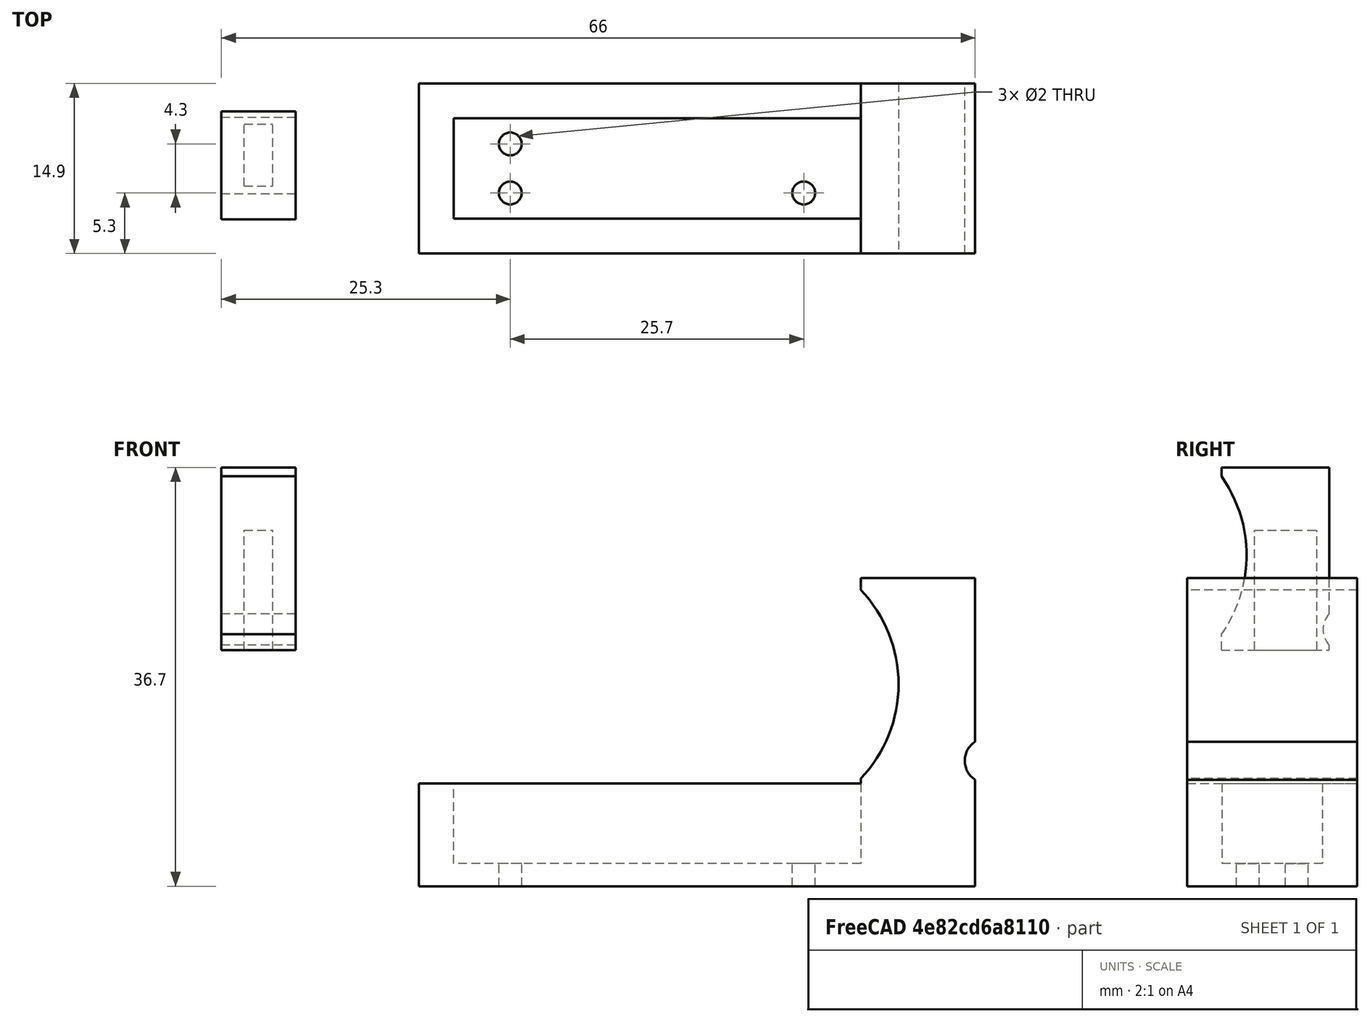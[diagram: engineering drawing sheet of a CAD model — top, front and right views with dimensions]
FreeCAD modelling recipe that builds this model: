
FCSTD DOCUMENT  (FreeCAD 0.18.4R)
Label: LDS_bracket_v1
License: All rights reserved
LicenseURL: http://en.wikipedia.org/wiki/All_rights_reserved
objects: Part::Cut×7, Part::Cylinder×7, Part::Box×6, Part::MultiFuse×2
note: 22 computed .brp shape members not serialized (recipe doc carries the construction recipe); baked Part::Feature solids carry a one-line shape summary decoded from their .brp

FEATURE [Part::Box] Box  label="Cube"
  AttacherType = Attacher::AttachEngine3D
  Height = 10
  Length = 36.6
  Placement = pos=(0.05,0.05,-2) rot=(0,0,1;0rad)
  Width = 8.8
FEATURE [Part::Box] Box001  label="Cube001"
  AttacherType = Attacher::AttachEngine3D
  Height = 7
  Length = 45.7
  Placement = pos=(-3,-3,0) rot=(0,0,1;0rad)
  Width = 14.9
FEATURE [Part::Cut] Cut
  Base = -> Box001
  Tool = -> Box
FEATURE [Part::Box] Box004  label="Cube004"
  AttacherType = Attacher::AttachEngine3D
  Height = 2
  Length = 45.7
  Placement = pos=(-3,-3,-2) rot=(0,0,1;0rad)
  Width = 14.9
FEATURE [Part::Cylinder] Cylinder
  Angle = 360
  AttacherType = Attacher::AttachEngine3D
  Height = 10
  Placement = pos=(5,2.3,-4) rot=(0,0,1;0rad)
  Radius = 1
FEATURE [Part::Cylinder] Cylinder002
  Angle = 360
  AttacherType = Attacher::AttachEngine3D
  Height = 10
  Placement = pos=(5,6.6,-4) rot=(0,0,1;0rad)
  Radius = 1
FEATURE [Part::Cylinder] Cylinder003
  Angle = 360
  AttacherType = Attacher::AttachEngine3D
  Height = 10
  Placement = pos=(30.7,2.3,-4) rot=(0,0,1;0rad)
  Radius = 1
FEATURE [Part::Box] Box005  label="Cube005"
  AttacherType = Attacher::AttachEngine3D
  Height = 27
  Length = 10
  Placement = pos=(35.7,-3,-2) rot=(0,0,1;0rad)
  Width = 14.9
FEATURE [Part::Cylinder] Cylinder004
  Angle = 360
  AttacherType = Attacher::AttachEngine3D
  Height = 20
  Placement = pos=(27,14,15.7) rot=(1,0,0;1.5708rad)
  Radius = 12
FEATURE [Part::Cut] Cut001
  Base = -> Box005
  Tool = -> Cylinder004
FEATURE [Part::Cylinder] Cylinder005
  Angle = 360
  AttacherType = Attacher::AttachEngine3D
  Height = 16
  Placement = pos=(46.8,-3.5,9) rot=(-1,0,0;1.5708rad)
  Radius = 2
FEATURE [Part::Cut] Cut002
  Base = -> Cut001
  Tool = -> Cylinder005
FEATURE [Part::MultiFuse] Fusion
  Shapes = -> [Cylinder,Cylinder002,Cylinder003]
FEATURE [Part::MultiFuse] Fusion001
  Shapes = -> [Cut,Cut002,Box004]
FEATURE [Part::Cut] Cut003
  Base = -> Fusion001
  Tool = -> Fusion
FEATURE [Part::Box] Box007  label="Cube007"
  AttacherType = Attacher::AttachEngine3D
  Height = 10.5
  Length = 2.5
  Placement = pos=(-18.3,2.9,18.7) rot=(0,0,1;0rad)
  Width = 5.45
FEATURE [Part::Box] Box008  label="Cube008"
  AttacherType = Attacher::AttachEngine3D
  Height = 16
  Length = 6.5
  Placement = pos=(-20.3,0,18.7) rot=(0,0,1;0rad)
  Width = 9.45
FEATURE [Part::Cut] Cut004
  Base = -> Box008
  Tool = -> Box007
FEATURE [Part::Cylinder] Cylinder006
  Angle = 360
  AttacherType = Attacher::AttachEngine3D
  Height = 16
  Placement = pos=(-10,-9.8,27) rot=(0,-1,0;1.5708rad)
  Radius = 12
FEATURE [Part::Cut] Cut005
  Base = -> Cut004
  Tool = -> Cylinder006
FEATURE [Part::Cylinder] Cylinder007
  Angle = 360
  AttacherType = Attacher::AttachEngine3D
  Height = 10
  Placement = pos=(-12,10.9,20.5) rot=(0,-1,0;1.5708rad)
  Radius = 2
FEATURE [Part::Cut] Cut006
  Base = -> Cut005
  Tool = -> Cylinder007
